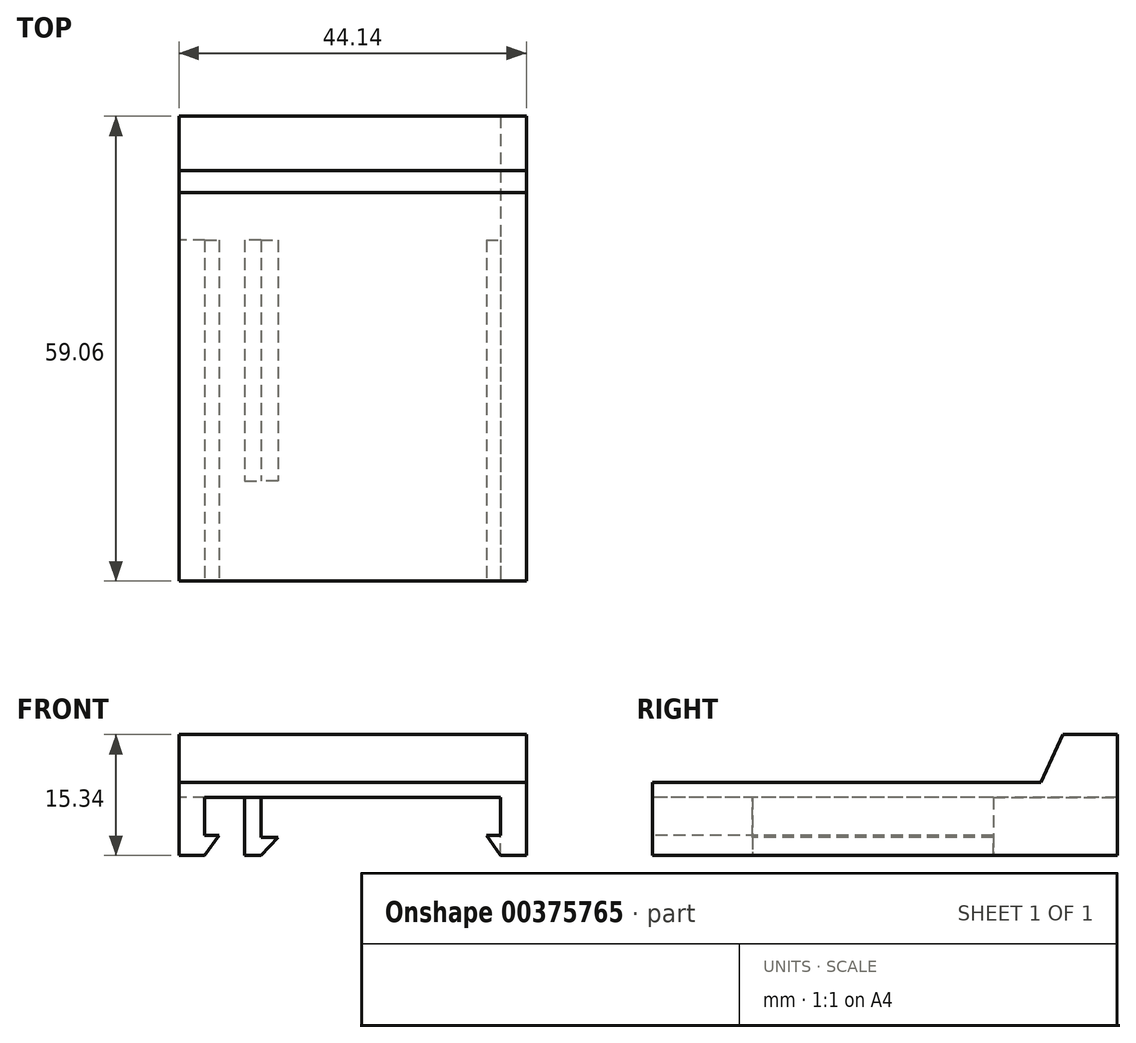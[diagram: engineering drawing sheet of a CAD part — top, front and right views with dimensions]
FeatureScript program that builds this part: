
annotation { "Feature Type Name" : "Feature", "Feature Type Description" : "" }
export const myFeature = defineFeature(function(context is Context, id is Id, definition is map)
    precondition{}
    {
        {
            var Q0;
            Q0=qCreatedBy(makeId("Front.planeOp"),FACE);
            var sketch = newSketch(context, id + "F0", { "sketchPlane" : qUnion([Q0])});
            skLineSegment(sketch, "E0.bottom", {"start": v(22.07, 4.62) * mm, "end": v(-22.07, 4.62) * mm});
            skLineSegment(sketch, "E0.top", {"start": v(22.07, -4.62) * mm, "end": v(-22.07, -4.62) * mm});
            skLineSegment(sketch, "E0.left", {"start": v(22.07, 4.62) * mm, "end": v(22.07, -4.62) * mm});
            skLineSegment(sketch, "E0.right", {"start": v(-22.07, 4.62) * mm, "end": v(-22.07, -4.62) * mm});
            skPoint(sketch, "E0.middle", {"position": v(0, 0) * mm});
            skSolve(sketch);
        }
        {
            var Q0;
            Q0=makeQuery(id+"F0.imprint","IMPRINT",FACE,{"disambiguationData":[TD([[makeQuery(id+"F0.imprint","IMPRINT",EDGE,{"derivedFrom":sQuery(id+"F0.wireOp",EDGE,"E0.bottom")}),1.0]])]});
            extrude(context, id + "F1", {"entities" : qUnion([Q0]), "oppositeDirection" : true, "depth" : 59.05 * mm});
        }
        {
            var Q0;
            Q0=makeQuery(id+"F1.opExtrude","SWEPT_FACE",FACE,{"disambiguationData":[OSD([sQuery(id+"F0.wireOp",EDGE,"E0.bottom")])]});
            var sketch = newSketch(context, id + "F2", { "sketchPlane" : qUnion([Q0])});
            skLineSegment(sketch, "E1.bottom", {"start": v(-22.07, 59.06) * mm, "end": v(22.07, 59.06) * mm});
            skLineSegment(sketch, "E1.top", {"start": v(-22.07, 49.35) * mm, "end": v(22.07, 49.35) * mm});
            skLineSegment(sketch, "E1.left", {"start": v(-22.07, 59.06) * mm, "end": v(-22.07, 49.35) * mm});
            skLineSegment(sketch, "E1.right", {"start": v(22.07, 59.06) * mm, "end": v(22.07, 49.35) * mm});
            skSolve(sketch);
        }
        {
            var Q0;
            Q0 = qSketchRegion(id + "F2", true);
            extrude(context, id + "F3", {"entities" : qUnion([Q0]), "operationType" : NewBodyOperationType.ADD, "depth" : 6.1 * mm});
        }
        {
            var Q0;
            Q0=makeQuery(id+"F1.opExtrude","CAP_FACE",FACE,{"disambiguationData":[OSD([sQuery(id+"F0.wireOp",EDGE,"E0.bottom"),sQuery(id+"F0.wireOp",EDGE,"E0.top"),sQuery(id+"F0.wireOp",EDGE,"E0.left"),sQuery(id+"F0.wireOp",EDGE,"E0.right")])],"isStart":true});
            var sketch = newSketch(context, id + "F4", { "sketchPlane" : qUnion([Q0])});
            skPoint(sketch, "E2.middle", {"position": v(0, 0) * mm});
            skLineSegment(sketch, "E3.top", {"start": v(-13.72, -4.62) * mm, "end": v(-11.66, -4.62) * mm});
            skLineSegment(sketch, "E3.left", {"start": v(-13.72, 2.74) * mm, "end": v(-13.72, -4.62) * mm});
            skLineSegment(sketch, "E4", {"start": v(-11.66, -4.62) * mm, "end": v(-9.47, -2.34) * mm});
            skLineSegment(sketch, "E5", {"start": v(-9.47, -2.34) * mm, "end": v(-11.66, -2.34) * mm});
            skLineSegment(sketch, "E6", {"start": v(-18.8, -4.62) * mm, "end": v(-17, -2.08) * mm});
            skLineSegment(sketch, "E7", {"start": v(-17, -2.08) * mm, "end": v(-18.8, -2.08) * mm});
            skLineSegment(sketch, "E8", {"start": v(18.8, -2.08) * mm, "end": v(17, -2.08) * mm});
            skLineSegment(sketch, "E9", {"start": v(17, -2.08) * mm, "end": v(18.8, -4.62) * mm});
            skLineSegment(sketch, "E10", {"start": v(-18.8, 2.74) * mm, "end": v(-13.72, 2.74) * mm});
            skLineSegment(sketch, "E11", {"start": v(-11.66, 2.74) * mm, "end": v(18.8, 2.74) * mm});
            skLineSegment(sketch, "E12", {"start": v(-11.66, 2.74) * mm, "end": v(-11.66, -2.34) * mm});
            skLineSegment(sketch, "E13", {"start": v(-18.8, 2.74) * mm, "end": v(-18.8, -2.08) * mm});
            skLineSegment(sketch, "E14", {"start": v(-22.07, -4.62) * mm, "end": v(-18.8, -4.62) * mm});
            skLineSegment(sketch, "E15", {"start": v(18.8, 2.74) * mm, "end": v(18.8, -2.08) * mm});
            skSolve(sketch);
        }
        {
            var Q0;
            {var subQ1=sQuery(id+"F4.wireOp",EDGE,"E4");Q0=makeQuery(id+"F4.imprint","IMPRINT",FACE,{"disambiguationData":[TD([[makeQuery(id+"F4.imprint","IMPRINT",EDGE,{"derivedFrom":subQ1}),-1.0]])]});}
            extrude(context, id + "F5", {"entities" : qUnion([Q0]), "operationType" : NewBodyOperationType.REMOVE, "oppositeDirection" : true, "depth" : 81.03 * mm});
        }
        {
            var Q0;
            {var subQ0=sQuery(id+"F4.wireOp",EDGE,"E3.left");Q0=makeQuery(id+"F4.imprint","IMPRINT",FACE,{"disambiguationData":[TD([[makeQuery(id+"F4.imprint","IMPRINT",EDGE,{"derivedFrom":subQ0}),-1.0]])]});}
            var Q1;
            {var subQ1=sQuery(id+"F4.wireOp",EDGE,"E4");Q1=makeQuery(id+"F4.imprint","IMPRINT",FACE,{"disambiguationData":[TD([[makeQuery(id+"F4.imprint","IMPRINT",EDGE,{"derivedFrom":subQ1}),-1.0]])]});}
            extrude(context, id + "F6", {"entities" : qUnion([Q0, Q1]), "operationType" : NewBodyOperationType.REMOVE, "oppositeDirection" : true, "depth" : 82.3 * mm});
        }
        {
            var Q0;
            Q0=makeQuery(id+"F3.boolean.opBoolean","MERGE",FACE,{"derivedFrom":[makeQuery(id+"F1.opExtrude","SWEPT_FACE",FACE,{"disambiguationData":[OSD([sQuery(id+"F0.wireOp",EDGE,"E0.right")])]}),makeQuery(id+"F3.opExtrude","SWEPT_FACE",FACE,{"disambiguationData":[OSD([sQuery(id+"F2.wireOp",EDGE,"E1.left")])]})]});
            var sketch = newSketch(context, id + "F7", { "sketchPlane" : qUnion([Q0])});
            skLineSegment(sketch, "E16", {"start": v(-49.35, 4.62) * mm, "end": v(-52.18, 10.72) * mm});
            skLineSegment(sketch, "E17", {"start": v(-52.18, 10.72) * mm, "end": v(-49.35, 10.72) * mm});
            skLineSegment(sketch, "E18", {"start": v(-49.35, 10.72) * mm, "end": v(-49.35, 4.62) * mm});
            skSolve(sketch);
        }
        {
            var Q0;
            Q0=makeQuery(id+"F7.imprint","IMPRINT",FACE,{"disambiguationData":[TD([[makeQuery(id+"F7.imprint","IMPRINT",EDGE,{"derivedFrom":sQuery(id+"F7.wireOp",EDGE,"E16")}),-1.0]])]});
            extrude(context, id + "F8", {"entities" : qUnion([Q0]), "operationType" : NewBodyOperationType.REMOVE, "oppositeDirection" : true, "depth" : 67.56 * mm});
        }
        {
            var Q0;
            Q0=makeQuery(id+"F3.boolean.opBoolean","MERGE",FACE,{"derivedFrom":[makeQuery(id+"F1.opExtrude","CAP_FACE",FACE,{"disambiguationData":[OSD([sQuery(id+"F0.wireOp",EDGE,"E0.bottom"),sQuery(id+"F0.wireOp",EDGE,"E0.top"),sQuery(id+"F0.wireOp",EDGE,"E0.left"),sQuery(id+"F0.wireOp",EDGE,"E0.right")])],"isStart":false}),makeQuery(id+"F3.opExtrude","SWEPT_FACE",FACE,{"disambiguationData":[OSD([sQuery(id+"F2.wireOp",EDGE,"E1.bottom")])]})]});
            var sketch = newSketch(context, id + "F9", { "sketchPlane" : qUnion([Q0])});
            skLineSegment(sketch, "E19.bottom", {"start": v(-18.8, -4.62) * mm, "end": v(22.07, -4.62) * mm});
            skLineSegment(sketch, "E19.top", {"start": v(-18.8, 2.74) * mm, "end": v(22.07, 2.74) * mm});
            skLineSegment(sketch, "E19.left", {"start": v(-18.8, -4.62) * mm, "end": v(-18.8, 2.74) * mm});
            skLineSegment(sketch, "E19.right", {"start": v(22.07, -4.62) * mm, "end": v(22.07, 2.74) * mm});
            skSolve(sketch);
        }
        {
            var Q0;
            Q0 = qSketchRegion(id + "F9", true);
            extrude(context, id + "F10", {"entities" : qUnion([Q0]), "operationType" : NewBodyOperationType.REMOVE, "oppositeDirection" : true, "depth" : 15.75 * mm});
        }
        {
            var Q0;
            Q0=makeQuery(id+"F1.opExtrude","CAP_FACE",FACE,{"disambiguationData":[OSD([sQuery(id+"F0.wireOp",EDGE,"E0.bottom"),sQuery(id+"F0.wireOp",EDGE,"E0.top"),sQuery(id+"F0.wireOp",EDGE,"E0.left"),sQuery(id+"F0.wireOp",EDGE,"E0.right")])],"isStart":true});
            var sketch = newSketch(context, id + "F11", { "sketchPlane" : qUnion([Q0])});
            skLineSegment(sketch, "E20.bottom", {"start": v(-13.72, -4.62) * mm, "end": v(-6.98, -4.62) * mm});
            skLineSegment(sketch, "E20.top", {"start": v(-13.72, 2.74) * mm, "end": v(-6.98, 2.74) * mm});
            skLineSegment(sketch, "E20.left", {"start": v(-13.72, -4.62) * mm, "end": v(-13.72, 2.74) * mm});
            skLineSegment(sketch, "E20.right", {"start": v(-6.98, -4.62) * mm, "end": v(-6.98, 2.74) * mm});
            skSolve(sketch);
        }
        {
            var Q0;
            Q0 = qSketchRegion(id + "F11", true);
            extrude(context, id + "F12", {"entities" : qUnion([Q0]), "operationType" : NewBodyOperationType.REMOVE, "oppositeDirection" : true, "depth" : 12.7 * mm});
        }
        {
            var Q0;
            Q0=makeQuery(id+"F1.opExtrude","SWEPT_BODY",BODY,{"disambiguationData":[OSD([sQuery(id+"F0.wireOp",EDGE,"E0.bottom"),sQuery(id+"F0.wireOp",EDGE,"E0.top"),sQuery(id+"F0.wireOp",EDGE,"E0.left"),sQuery(id+"F0.wireOp",EDGE,"E0.right")])]});
            var Q1;
            Q1=qCreatedBy(makeId("Right.planeOp"),FACE);
            mirror(context, id + "F13", {"entities" : qUnion([Q0]), "mirrorPlane" : qUnion([Q1])});
        }
        {
            var Q0;
            Q0=makeQuery(id+"F1.opExtrude","SWEPT_BODY",BODY,{"disambiguationData":[OSD([sQuery(id+"F0.wireOp",EDGE,"E0.bottom"),sQuery(id+"F0.wireOp",EDGE,"E0.top"),sQuery(id+"F0.wireOp",EDGE,"E0.left"),sQuery(id+"F0.wireOp",EDGE,"E0.right")])]});
            deleteBodies(context, id + "F14", {"entities" : qUnion([Q0])});
        }
        {
            var Q0;
            Q0=makeQuery(id+"F13.opPattern","COPY",BODY,{"derivedFrom":makeQuery(id+"F1.opExtrude","SWEPT_BODY",BODY,{"disambiguationData":[OSD([sQuery(id+"F0.wireOp",EDGE,"E0.bottom"),sQuery(id+"F0.wireOp",EDGE,"E0.top"),sQuery(id+"F0.wireOp",EDGE,"E0.left"),sQuery(id+"F0.wireOp",EDGE,"E0.right")])]}),"instanceName":"1"});
            var Q1;
            Q1=qCreatedBy(makeId("Right.planeOp"),FACE);
            mirror(context, id + "F15", {"entities" : qUnion([Q0]), "mirrorPlane" : qUnion([Q1])});
        }
        {
            var Q0;
            Q0=makeQuery(id+"F13.opPattern","COPY",BODY,{"derivedFrom":makeQuery(id+"F1.opExtrude","SWEPT_BODY",BODY,{"disambiguationData":[OSD([sQuery(id+"F0.wireOp",EDGE,"E0.bottom"),sQuery(id+"F0.wireOp",EDGE,"E0.top"),sQuery(id+"F0.wireOp",EDGE,"E0.left"),sQuery(id+"F0.wireOp",EDGE,"E0.right")])]}),"instanceName":"1"});
            deleteBodies(context, id + "F16", {"entities" : qUnion([Q0])});
        }
    });
